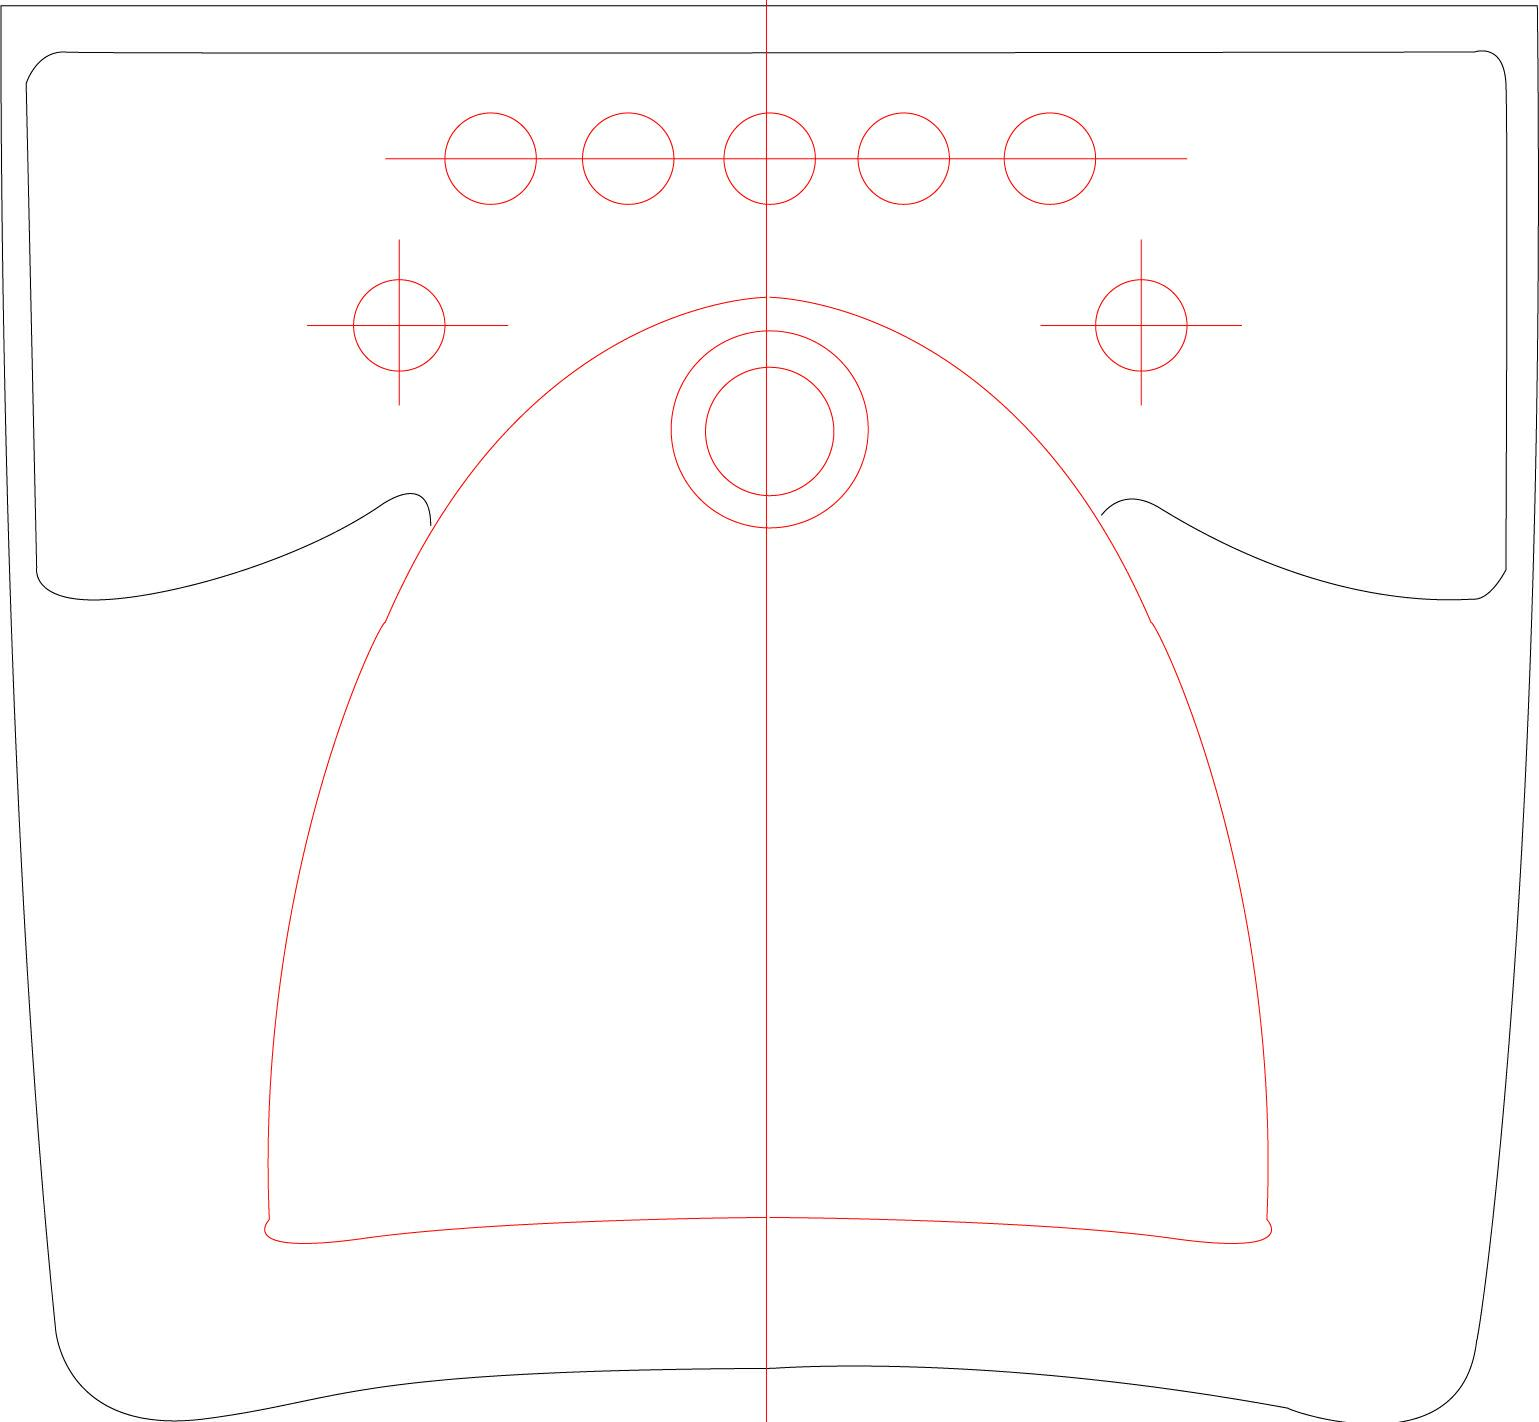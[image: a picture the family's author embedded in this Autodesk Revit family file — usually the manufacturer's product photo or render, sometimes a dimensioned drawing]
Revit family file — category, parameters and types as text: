
# Revit family: 01291  LVM Aquajet
name_source: partatom
category: Aparatos sanitarios
revit_build: Autodesk Revit 2016 (Build: 20151007_0715(x64)
units: mm (PartAtom-declared; Revit-internal decimal feet)

## family parameters
Anfitrión = Muro
Compartido = No
Corte con vacíos al cargar = No
Cota de conector redondo = Diámetro de uso
Número OmniClass = 23.45.00.00
Punto de cálculo de habitación = No
Siempre vertical = Sí
Tipo de pieza = Normal
Título OmniClass = Sanitary, Laundry, and Cleaning Equipment

## types (1)
- Tipo 1
    Acabado = Brillante
    Alto Nominal = 135 mm  [stored 0.442913 ft]
    Ancho Nominal = 512 mm  [stored 1.67979 ft]
    Característica = Lavamanos con amplia superficie de repisa para ubicar artículos de aseo, frente concavo para facilitar el acceso a personas con silla de ruedas, Agujeros insunuados que permiten escoger diferentes opciones de grifería, Agujero integral de drenaje que evita rebose, Requiere brazos para su instaación y cumplimiento de norma.
    Color = Blanco
    Cumplimiento de Norma = NTC 920.1 Aparatos sanitarios de porcelana vitrificada / ASME A 112.19.2 / CSA B 45.1 / NOM 009 / 010 Norma oficial Mexicana / Centro de Estudios de Medición y Certificación de calidad de Chile / Requerimientos para discapacitados cuendo se instala correctamente, según recomendaciones de CORONA
    Código de montaje = D2010
    Descripción = Lavamanos de Colgar accesible para aplicaciones en destinos público y salud
    Descripción de la garantía = Garantía integral de por vida Corona
    Diámetro de conexión de entrada = 1/2"
    Diámetro de conexión sanitaria = 2"
    Duración Garantía Unidad = años
    Fabricante = www.corona.com.co
    Forma = Rectangular
    Información del producto = https://www.corona.co
    Longitud Nominal = 501 mm  [stored 1.6437 ft]
    Material = Ceramica_Corona_Blanco
    Material Secundario = Plastico_Corona_Blanco
    Nombre = Lavamanos Aquajet
    Numero de Modelo = 01291
    Requerimientos de Accesibilidad = Necesita
    Responsable Garantia Partes = www.corona.com.co
    Tamaño = 501 x 512 x 135 mm
    Tipo de Activo = Fijo
    Tráfico = Institucional Alto tráfico

note: [stored X ft] marks values corroborated as IEEE doubles in the binary element streams (Revit-internal decimal feet)
